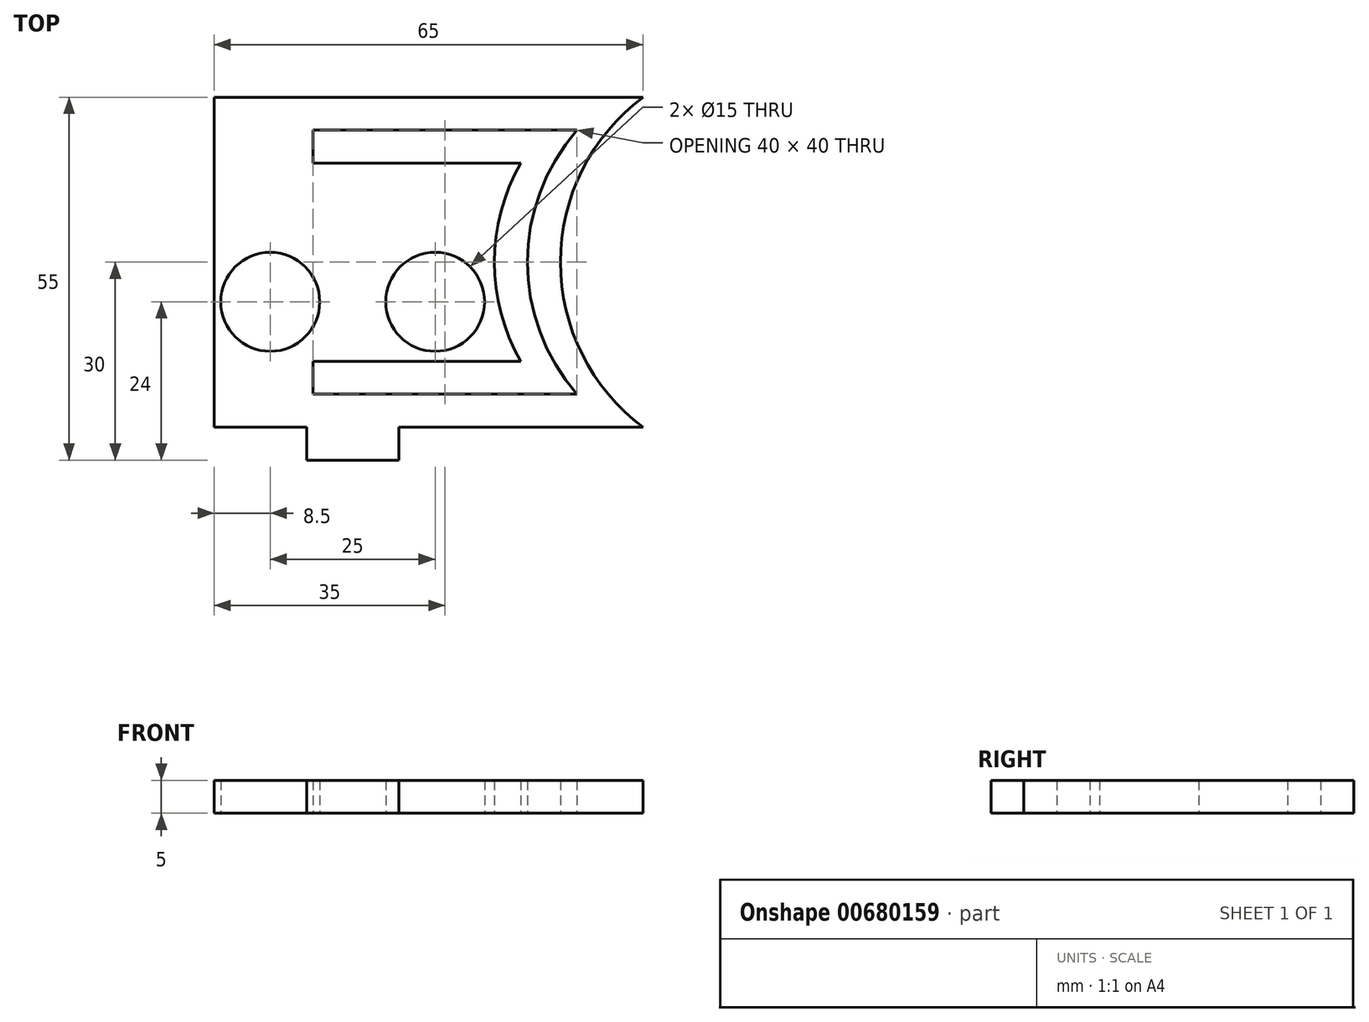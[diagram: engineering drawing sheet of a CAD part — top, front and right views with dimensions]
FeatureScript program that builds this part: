
annotation { "Feature Type Name" : "Feature", "Feature Type Description" : "" }
export const myFeature = defineFeature(function(context is Context, id is Id, definition is map)
    precondition{}
    {
        {
            var Q0;
            Q0=qCreatedBy(makeId("Top.planeOp"),FACE);
            var sketch = newSketch(context, id + "F0", { "sketchPlane" : qUnion([Q0])});
            skLineSegment(sketch, "E0.bottom", {"start": v(-32.5, 25) * mm, "end": v(32.5, 25) * mm});
            skLineSegment(sketch, "E0.top", {"start": v(-32.5, -25) * mm, "end": v(-18.5, -25) * mm});
            skLineSegment(sketch, "E0.left", {"start": v(-32.5, 25) * mm, "end": v(-32.5, -25) * mm});
            skArc(sketch, "E1", {"start": v(32.5, 25) * mm, "mid": v(20, 0) * mm, "end": v(32.5, -25) * mm});
            skArc(sketch, "E2", {"start": v(22.5, 20) * mm, "mid": v(15, 0) * mm, "end": v(22.5, -20) * mm});
            skLineSegment(sketch, "E3.bottom", {"start": v(22.5, 20) * mm, "end": v(22.5, 20) * mm});
            skLineSegment(sketch, "E3.top", {"start": v(22.5, -20) * mm, "end": v(22.5, -20) * mm});
            skArc(sketch, "E4", {"start": v(13.96, 15) * mm, "mid": v(10, 0) * mm, "end": v(13.96, -15) * mm});
            skLineSegment(sketch, "E5", {"start": v(-17.5, 20) * mm, "end": v(22.5, 20) * mm});
            skLineSegment(sketch, "E6", {"start": v(-17.5, 20) * mm, "end": v(-17.5, 15) * mm});
            skLineSegment(sketch, "E7", {"start": v(-17.5, 15) * mm, "end": v(13.96, 15) * mm});
            skLineSegment(sketch, "E8", {"start": v(-17.5, -20) * mm, "end": v(22.5, -20) * mm});
            skLineSegment(sketch, "E9", {"start": v(-17.5, -20) * mm, "end": v(-17.5, -15) * mm});
            skLineSegment(sketch, "E10", {"start": v(-17.5, -15) * mm, "end": v(13.96, -15) * mm});
            skLineSegment(sketch, "E11", {"start": v(-24, -25) * mm, "end": v(-11.5, -25) * mm});
            skLineSegment(sketch, "E12", {"start": v(-11.5, -25) * mm, "end": v(-4.5, -25) * mm});
            skLineSegment(sketch, "E13", {"start": v(-18.5, -25) * mm, "end": v(-18.5, -30) * mm});
            skLineSegment(sketch, "E14", {"start": v(-18.5, -30) * mm, "end": v(-4.5, -30) * mm});
            skLineSegment(sketch, "E15", {"start": v(-4.5, -30) * mm, "end": v(-4.5, -25) * mm});
            skLineSegment(sketch, "E16.trimOffspring", {"start": v(-4.5, -25) * mm, "end": v(32.5, -25) * mm});
            skCircle(sketch, "E17", {"center": v(-24, -6) * mm, "radius": 7.5 * mm});
            skCircle(sketch, "E18", {"center": v(1, -6) * mm, "radius": 7.5 * mm});
            skSolve(sketch);
        }
        {
            var Q0;
            {var subQ1=sQuery(id+"F0.wireOp",EDGE,"E12");Q0=makeQuery(id+"F0.imprint","IMPRINT",FACE,{"disambiguationData":[TD([[makeQuery(id+"F0.imprint","IMPRINT",EDGE,{"derivedFrom":subQ1}),-1.0]])]});}
            var Q1;
            Q1=makeQuery(id+"F0.imprint","IMPRINT",FACE,{"disambiguationData":[TD([[makeQuery(id+"F0.imprint","IMPRINT",EDGE,{"derivedFrom":sQuery(id+"F0.wireOp",EDGE,"E0.bottom")}),-1.0]])]});
            extrude(context, id + "F1", {"entities" : qUnion([Q0, Q1]), "depth" : 5 * mm, "offsetDistance" : 25 * mm});
        }
    });
